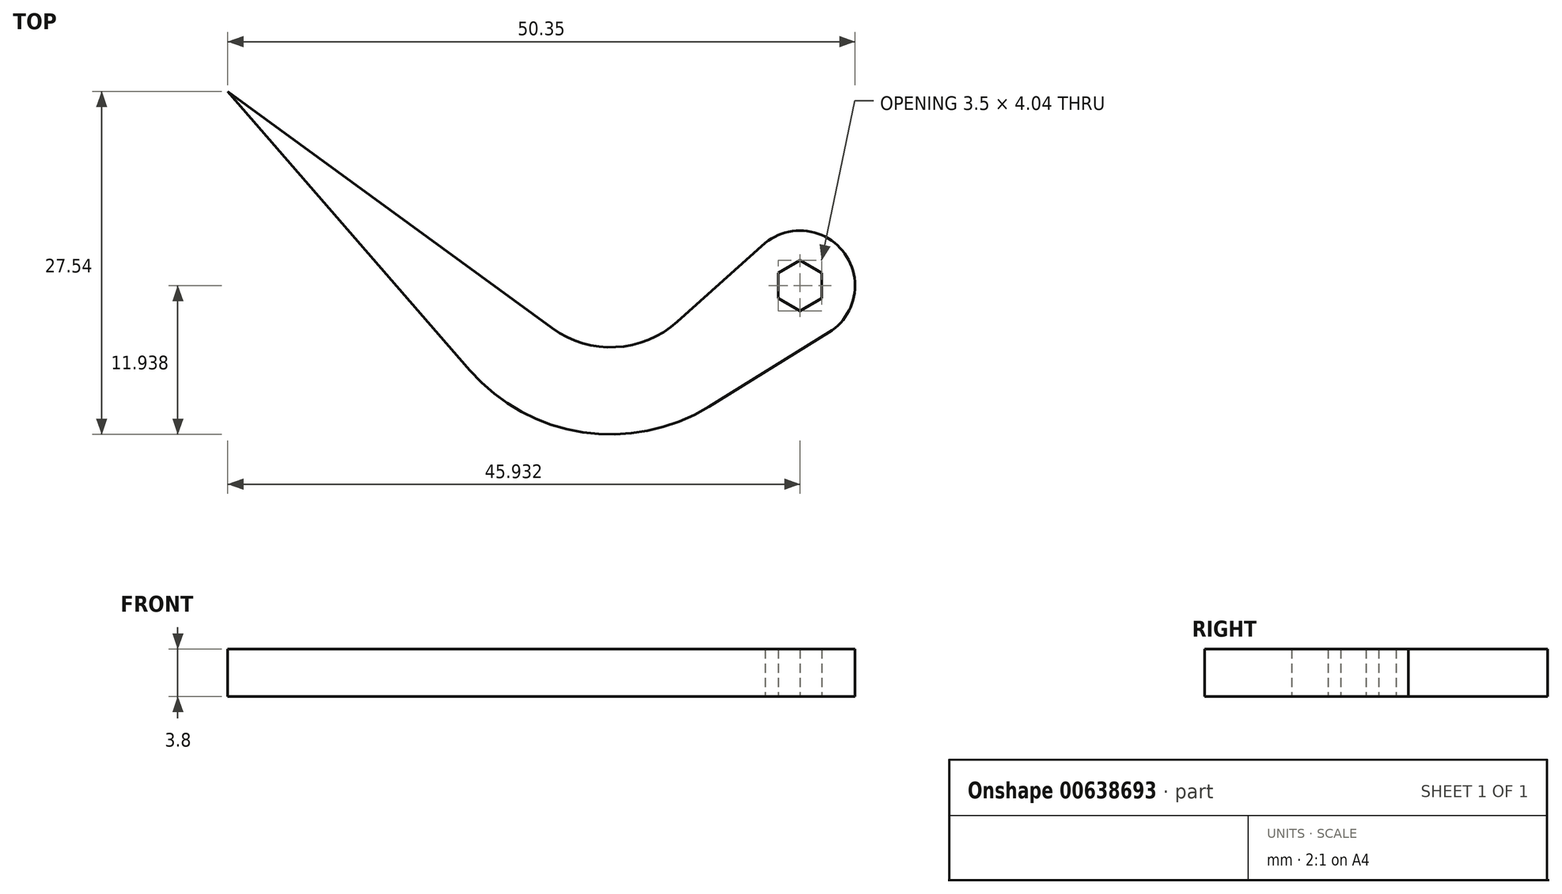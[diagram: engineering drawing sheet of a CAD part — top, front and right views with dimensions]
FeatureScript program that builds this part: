
annotation { "Feature Type Name" : "Feature", "Feature Type Description" : "" }
export const myFeature = defineFeature(function(context is Context, id is Id, definition is map)
    precondition{}
    {
        {
            var Q0;
            Q0=qCreatedBy(makeId("Top.planeOp"),FACE);
            var sketch = newSketch(context, id + "F0", { "sketchPlane" : qUnion([Q0])});
            skLineSegment(sketch, "E0", {"start": v(-7.05, -6.32) * mm, "end": v(0, 0) * mm});
            skLineSegment(sketch, "E1", {"start": v(5.11, -7.18) * mm, "end": v(-4.5, -13.12) * mm});
            skArc(sketch, "E2", {"start": v(5.11, -7.18) * mm, "mid": v(6.39, -0.86) * mm, "end": v(0, 0) * mm});
            skLineSegment(sketch, "E3", {"start": v(-17.1, -6.83) * mm, "end": v(-43.14, 12.18) * mm});
            skLineSegment(sketch, "E4", {"start": v(-43.14, 12.18) * mm, "end": v(-23.72, -10.2) * mm});
            skPoint(sketch, "E5.visualSharp", {"position": v(-11.87, -10.65) * mm});
            skArc(sketch, "E5.filletArc", {"start": v(-17.1, -6.83) * mm, "mid": v(-11.99, -8.35) * mm, "end": v(-7.05, -6.32) * mm});
            skPoint(sketch, "E6.visualSharp", {"position": v(-15.35, -19.83) * mm});
            skArc(sketch, "E6.filletArc", {"start": v(-23.72, -10.2) * mm, "mid": v(-14.65, -15.2) * mm, "end": v(-4.5, -13.12) * mm});
            skCircle(sketch, "E7.cCircle", {"center": v(2.8, -3.42) * mm, "radius": 1.75 * mm, "construction": true});
            skLineSegment(sketch, "E7.0", {"start": v(1.04, -4.43) * mm, "end": v(1.04, -2.41) * mm});
            skLineSegment(sketch, "E7.1", {"start": v(1.04, -2.41) * mm, "end": v(2.8, -1.4) * mm});
            skLineSegment(sketch, "E7.2", {"start": v(2.8, -1.4) * mm, "end": v(4.54, -2.41) * mm});
            skLineSegment(sketch, "E7.3", {"start": v(4.54, -2.41) * mm, "end": v(4.54, -4.43) * mm});
            skLineSegment(sketch, "E7.4", {"start": v(4.54, -4.43) * mm, "end": v(2.8, -5.44) * mm});
            skLineSegment(sketch, "E7.5", {"start": v(2.8, -5.44) * mm, "end": v(1.04, -4.43) * mm});
            skPoint(sketch, "E7.0.midPoint", {"position": v(1.04, -3.42) * mm});
            skSolve(sketch);
        }
        {
            var Q0;
            Q0=makeQuery(id+"F0.imprint","IMPRINT",FACE,{"disambiguationData":[TD([[makeQuery(id+"F0.imprint","IMPRINT",EDGE,{"derivedFrom":sQuery(id+"F0.wireOp",EDGE,"E0")}),-1.0]])]});
            extrude(context, id + "F1", {"entities" : qUnion([Q0]), "depth" : 3.8 * mm, "offsetDistance" : 25 * mm});
        }
    });
